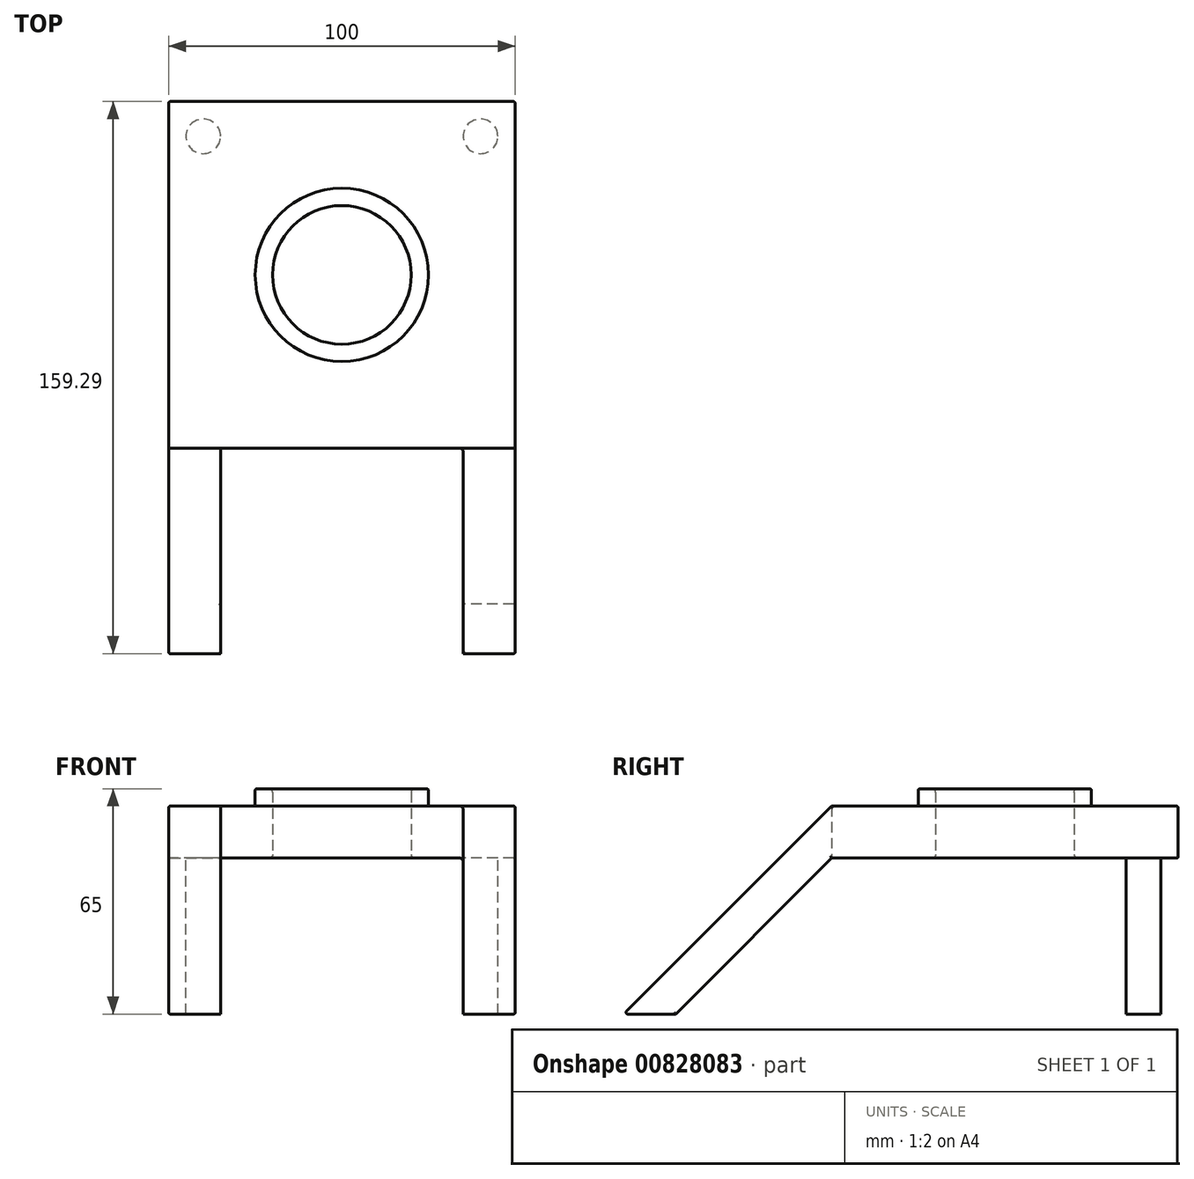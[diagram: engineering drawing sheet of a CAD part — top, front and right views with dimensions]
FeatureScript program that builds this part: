
annotation { "Feature Type Name" : "Feature", "Feature Type Description" : "" }
export const myFeature = defineFeature(function(context is Context, id is Id, definition is map)
    precondition{}
    {
        {
            var Q0;
            Q0=qCreatedBy(makeId("Top.planeOp"),FACE);
            var sketch = newSketch(context, id + "F0", { "sketchPlane" : qUnion([Q0])});
            skLineSegment(sketch, "E0.bottom", {"start": v(50, 50) * mm, "end": v(-50, 50) * mm});
            skLineSegment(sketch, "E0.top", {"start": v(50, -50) * mm, "end": v(-50, -50) * mm});
            skLineSegment(sketch, "E0.left", {"start": v(50, 50) * mm, "end": v(50, -50) * mm});
            skLineSegment(sketch, "E0.right", {"start": v(-50, 50) * mm, "end": v(-50, -50) * mm});
            skPoint(sketch, "E0.middle", {"position": v(0, 0) * mm});
            skCircle(sketch, "E1", {"center": v(0, 0) * mm, "radius": 25 * mm});
            skCircle(sketch, "E2.0", {"center": v(0, 0) * mm, "radius": 20 * mm});
            skCircle(sketch, "E3", {"center": v(-40, 40) * mm, "radius": 5 * mm});
            skCircle(sketch, "E4", {"center": v(40, 40) * mm, "radius": 5 * mm});
            skSolve(sketch);
        }
        {
            var Q0;
            Q0=makeQuery(id+"F0.imprint","IMPRINT",FACE,{"disambiguationData":[TD([[makeQuery(id+"F0.imprint","IMPRINT",EDGE,{"derivedFrom":sQuery(id+"F0.wireOp",EDGE,"E0.bottom")}),1.0]])]});
            var Q1;
            Q1=makeQuery(id+"F0.imprint","IMPRINT",FACE,{"disambiguationData":[TD([[makeQuery(id+"F0.imprint","IMPRINT",EDGE,{"derivedFrom":sQuery(id+"F0.wireOp",EDGE,"E4")}),1.0]])]});
            var Q2;
            Q2=makeQuery(id+"F0.imprint","IMPRINT",FACE,{"disambiguationData":[TD([[makeQuery(id+"F0.imprint","IMPRINT",EDGE,{"derivedFrom":sQuery(id+"F0.wireOp",EDGE,"E3")}),1.0]])]});
            extrude(context, id + "F1", {"entities" : qUnion([Q0, Q1, Q2]), "depth" : 15 * mm, "offsetDistance" : 25 * mm});
        }
        {
            var Q0;
            Q0=makeQuery(id+"F0.imprint","IMPRINT",FACE,{"disambiguationData":[TD([[makeQuery(id+"F0.imprint","IMPRINT",EDGE,{"derivedFrom":sQuery(id+"F0.wireOp",EDGE,"E1")}),1.0]])]});
            extrude(context, id + "F2", {"entities" : qUnion([Q0]), "operationType" : NewBodyOperationType.ADD, "depth" : 20 * mm, "offsetDistance" : 25 * mm});
        }
        {
            var Q0;
            Q0=makeQuery(id+"F0.imprint","IMPRINT",FACE,{"disambiguationData":[TD([[makeQuery(id+"F0.imprint","IMPRINT",EDGE,{"derivedFrom":sQuery(id+"F0.wireOp",EDGE,"E3")}),1.0]])]});
            var Q1;
            Q1=makeQuery(id+"F0.imprint","IMPRINT",FACE,{"disambiguationData":[TD([[makeQuery(id+"F0.imprint","IMPRINT",EDGE,{"derivedFrom":sQuery(id+"F0.wireOp",EDGE,"E4")}),1.0]])]});
            extrude(context, id + "F3", {"entities" : qUnion([Q0, Q1]), "operationType" : NewBodyOperationType.ADD, "oppositeDirection" : true, "depth" : 45 * mm, "offsetDistance" : 25 * mm});
        }
        {
            var Q0;
            Q0=qCreatedBy(makeId("Top.planeOp"),FACE);
            cPlane(context, id + "F4", {"entities" : qUnion([Q0]), "cplaneType" : CPlaneType.OFFSET, "offset" : 45 * mm, "oppositeDirection" : true, "width" : 150 * mm, "height" : 150 * mm});
        }
        {
            var Q0;
            Q0=qCreatedBy(id+"F4.planeOp",FACE);
            var sketch = newSketch(context, id + "F5", { "sketchPlane" : qUnion([Q0])});
            skLineSegment(sketch, "E5.0", {"start": v(50, -50) * mm, "end": v(-50, -50) * mm});
            skLineSegment(sketch, "E6.bottom", {"start": v(-50, -110) * mm, "end": v(-35, -110) * mm});
            skLineSegment(sketch, "E6.top", {"start": v(-50, -95) * mm, "end": v(-35, -95) * mm});
            skLineSegment(sketch, "E6.left", {"start": v(-50, -110) * mm, "end": v(-50, -95) * mm});
            skLineSegment(sketch, "E6.right", {"start": v(-35, -110) * mm, "end": v(-35, -95) * mm});
            skLineSegment(sketch, "E7.bottom", {"start": v(50, -95) * mm, "end": v(35, -95) * mm});
            skLineSegment(sketch, "E7.top", {"start": v(50, -110) * mm, "end": v(35, -110) * mm});
            skLineSegment(sketch, "E7.left", {"start": v(50, -95) * mm, "end": v(50, -110) * mm});
            skLineSegment(sketch, "E7.right", {"start": v(35, -95) * mm, "end": v(35, -110) * mm});
            skSolve(sketch);
        }
        {
            var Q0;
            Q0=qCreatedBy(makeId("Right.planeOp"),FACE);
            cPlane(context, id + "F6", {"entities" : qUnion([Q0]), "cplaneType" : CPlaneType.OFFSET, "offset" : 50 * mm, "width" : 150 * mm, "height" : 150 * mm});
        }
        {
            var Q0;
            Q0=qCreatedBy(id+"F6.planeOp",FACE);
            var sketch = newSketch(context, id + "F7", { "sketchPlane" : qUnion([Q0])});
            skPoint(sketch, "E8.0", {"position": v(-95, -45) * mm});
            skPoint(sketch, "E9.0", {"position": v(-50, 0) * mm});
            skPoint(sketch, "E10.0", {"position": v(-50, 15) * mm});
            skPoint(sketch, "E11.0", {"position": v(-110, -45) * mm});
            skLineSegment(sketch, "E12", {"start": v(-110, -45) * mm, "end": v(-50, 15) * mm});
            skSolve(sketch);
        }
        {
            var Q0;
            Q0=makeQuery(id+"F5.imprint","IMPRINT",FACE,{"disambiguationData":[TD([[makeQuery(id+"F5.imprint","IMPRINT",EDGE,{"derivedFrom":sQuery(id+"F5.wireOp",EDGE,"E7.bottom")}),1.0]])]});
            var Q1;
            Q1=sQuery(id+"F7.wireOp",EDGE,"E12");
            sweep(context, id + "F8", {"operationType" : NewBodyOperationType.ADD, "profiles" : qUnion([Q0]), "path" : qUnion([Q1])});
        }
        {
            var Q0;
            Q0=makeQuery(id+"F1.opExtrude","SWEPT_BODY",BODY,{"disambiguationData":[OSD([sQuery(id+"F0.wireOp",EDGE,"E0.bottom"),sQuery(id+"F0.wireOp",EDGE,"E0.top"),sQuery(id+"F0.wireOp",EDGE,"E0.left"),sQuery(id+"F0.wireOp",EDGE,"E0.right"),sQuery(id+"F0.wireOp",EDGE,"E1")])]});
            var Q1;
            Q1=qCreatedBy(makeId("Right.planeOp"),FACE);
            mirror(context, id + "F9", {"operationType" : NewBodyOperationType.ADD, "entities" : qUnion([Q0]), "mirrorPlane" : qUnion([Q1])});
        }
        {
            var Q0;
            Q0=makeQuery(id+"F9.opPattern","COPY",EDGE,{"derivedFrom":makeQuery(id+"F8.boolean.opBoolean","INTERSECT",EDGE,{"derivedFrom":[makeQuery(id+"F1.opExtrude","SWEPT_FACE",FACE,{"disambiguationData":[OSD([sQuery(id+"F0.wireOp",EDGE,"E0.top")])]}),makeQuery(id+"F8.opSweep","SWEPT_FACE",FACE,{"disambiguationData":[OSD([sQuery(id+"F5.wireOp",EDGE,"E7.right"),sQuery(id+"F7.wireOp",EDGE,"E12")])]})]}),"instanceName":"1"});
            var Q1;
            Q1=makeQuery(id+"F8.boolean.opBoolean","INTERSECT",EDGE,{"derivedFrom":[makeQuery(id+"F1.opExtrude","SWEPT_FACE",FACE,{"disambiguationData":[OSD([sQuery(id+"F0.wireOp",EDGE,"E0.top")])]}),makeQuery(id+"F8.opSweep","SWEPT_FACE",FACE,{"disambiguationData":[OSD([sQuery(id+"F5.wireOp",EDGE,"E7.right"),sQuery(id+"F7.wireOp",EDGE,"E12")])]})]});
            var Q2;
            Q2=makeQuery(id+"F2.opExtrude","SWEPT_FACE",FACE,{"disambiguationData":[OSD([sQuery(id+"F0.wireOp",EDGE,"E2.0")])]});
            fillet(context, id + "F10", {"entities" : qUnion([Q0, Q1, Q2]), "tangentPropagation" : true, "radius" : 1 * mm, "defaultsChanged" : true, "vertexSettings" : [], "allowEdgeOverflow" : false});
        }
        {
            var Q0;
            Q0=makeQuery(id+"F2.opExtrude","CAP_EDGE",EDGE,{"disambiguationData":[OSD([sQuery(id+"F0.wireOp",EDGE,"E1")])],"isStart":false});
            var Q1;
            Q1=makeQuery(id+"F1.opExtrude","CAP_EDGE",EDGE,{"disambiguationData":[OSD([sQuery(id+"F0.wireOp",EDGE,"E0.left")])],"isStart":false});
            var Q2;
            Q2=makeQuery(id+"F1.opExtrude","CAP_EDGE",EDGE,{"disambiguationData":[OSD([sQuery(id+"F0.wireOp",EDGE,"E0.bottom")])],"isStart":false});
            var Q3;
            Q3=makeQuery(id+"F1.opExtrude","SWEPT_EDGE",EDGE,{"disambiguationData":[OSD([sQuery(id+"F0.wireOp",EDGE,"E0.bottom"),sQuery(id+"F0.wireOp",EDGE,"E0.left")])]});
            var Q4;
            Q4=makeQuery(id+"F1.opExtrude","SWEPT_EDGE",EDGE,{"disambiguationData":[OSD([sQuery(id+"F0.wireOp",EDGE,"E0.bottom"),sQuery(id+"F0.wireOp",EDGE,"E0.right")])]});
            var Q5;
            Q5=makeQuery(id+"F1.opExtrude","CAP_EDGE",EDGE,{"disambiguationData":[OSD([sQuery(id+"F0.wireOp",EDGE,"E0.right")])],"isStart":false});
            var Q6;
            Q6=makeQuery(id+"F1.opExtrude","CAP_EDGE",EDGE,{"disambiguationData":[OSD([sQuery(id+"F0.wireOp",EDGE,"E0.right")])],"isStart":true});
            var Q7;
            Q7=makeQuery(id+"F1.opExtrude","CAP_EDGE",EDGE,{"disambiguationData":[OSD([sQuery(id+"F0.wireOp",EDGE,"E0.bottom")])],"isStart":true});
            var Q8;
            Q8=makeQuery(id+"F1.opExtrude","CAP_EDGE",EDGE,{"disambiguationData":[OSD([sQuery(id+"F0.wireOp",EDGE,"E0.left")])],"isStart":true});
            var Q9;
            Q9=makeQuery(id+"F8.opSweep","SWEPT_EDGE",EDGE,{"disambiguationData":[OSD([sQuery(id+"F5.wireOp",EDGE,"E7.bottom"),sQuery(id+"F5.wireOp",EDGE,"E7.left"),sQuery(id+"F7.wireOp",EDGE,"E12")])]});
            var Q10;
            Q10=makeQuery(id+"F8.opSweep","SWEPT_EDGE",EDGE,{"disambiguationData":[OSD([sQuery(id+"F5.wireOp",EDGE,"E7.top"),sQuery(id+"F5.wireOp",EDGE,"E7.left"),sQuery(id+"F7.wireOp",EDGE,"E12")])]});
            var Q11;
            Q11=makeQuery(id+"F9.opPattern","COPY",EDGE,{"derivedFrom":makeQuery(id+"F8.opSweep","SWEPT_EDGE",EDGE,{"disambiguationData":[OSD([sQuery(id+"F5.wireOp",EDGE,"E7.top"),sQuery(id+"F5.wireOp",EDGE,"E7.left"),sQuery(id+"F7.wireOp",EDGE,"E12")])]}),"instanceName":"1"});
            var Q12;
            Q12=makeQuery(id+"F9.opPattern","COPY",EDGE,{"derivedFrom":makeQuery(id+"F8.opSweep","SWEPT_EDGE",EDGE,{"disambiguationData":[OSD([sQuery(id+"F5.wireOp",EDGE,"E7.bottom"),sQuery(id+"F5.wireOp",EDGE,"E7.left"),sQuery(id+"F7.wireOp",EDGE,"E12")])]}),"instanceName":"1"});
            var Q13;
            Q13=makeQuery(id+"F9.opPattern","COPY",EDGE,{"derivedFrom":makeQuery(id+"F8.opSweep","CAP_EDGE",EDGE,{"disambiguationData":[OSD([sQuery(id+"F5.wireOp",EDGE,"E7.left"),sQuery(id+"F7.wireOp",VERTEX,"E12.start")])],"isStart":true}),"instanceName":"1"});
            var Q14;
            Q14=makeQuery(id+"F9.opPattern","COPY",EDGE,{"derivedFrom":makeQuery(id+"F8.opSweep","CAP_EDGE",EDGE,{"disambiguationData":[OSD([sQuery(id+"F5.wireOp",EDGE,"E7.bottom"),sQuery(id+"F7.wireOp",VERTEX,"E12.start")])],"isStart":true}),"instanceName":"1"});
            var Q15;
            Q15=makeQuery(id+"F9.opPattern","COPY",EDGE,{"derivedFrom":makeQuery(id+"F8.opSweep","CAP_EDGE",EDGE,{"disambiguationData":[OSD([sQuery(id+"F5.wireOp",EDGE,"E7.top"),sQuery(id+"F7.wireOp",VERTEX,"E12.start")])],"isStart":true}),"instanceName":"1"});
            var Q16;
            Q16=makeQuery(id+"F8.opSweep","CAP_EDGE",EDGE,{"disambiguationData":[OSD([sQuery(id+"F5.wireOp",EDGE,"E7.right"),sQuery(id+"F7.wireOp",VERTEX,"E12.start")])],"isStart":true});
            var Q17;
            Q17=makeQuery(id+"F8.opSweep","CAP_EDGE",EDGE,{"disambiguationData":[OSD([sQuery(id+"F5.wireOp",EDGE,"E7.top"),sQuery(id+"F7.wireOp",VERTEX,"E12.start")])],"isStart":true});
            var Q18;
            Q18=makeQuery(id+"F9.opPattern","COPY",EDGE,{"derivedFrom":makeQuery(id+"F8.opSweep","CAP_EDGE",EDGE,{"disambiguationData":[OSD([sQuery(id+"F5.wireOp",EDGE,"E7.right"),sQuery(id+"F7.wireOp",VERTEX,"E12.start")])],"isStart":true}),"instanceName":"1"});
            var Q19;
            Q19=makeQuery(id+"F8.opSweep","CAP_EDGE",EDGE,{"disambiguationData":[OSD([sQuery(id+"F5.wireOp",EDGE,"E7.left"),sQuery(id+"F7.wireOp",VERTEX,"E12.start")])],"isStart":true});
            fillet(context, id + "F11", {"entities" : qUnion([Q0, Q1, Q2, Q3, Q4, Q5, Q6, Q7, Q8, Q9, Q10, Q11, Q12, Q13, Q14, Q15, Q16, Q17, Q18, Q19]), "tangentPropagation" : true, "radius" : .5 * mm, "defaultsChanged" : false, "vertexSettings" : [], "allowEdgeOverflow" : false});
        }
    });
